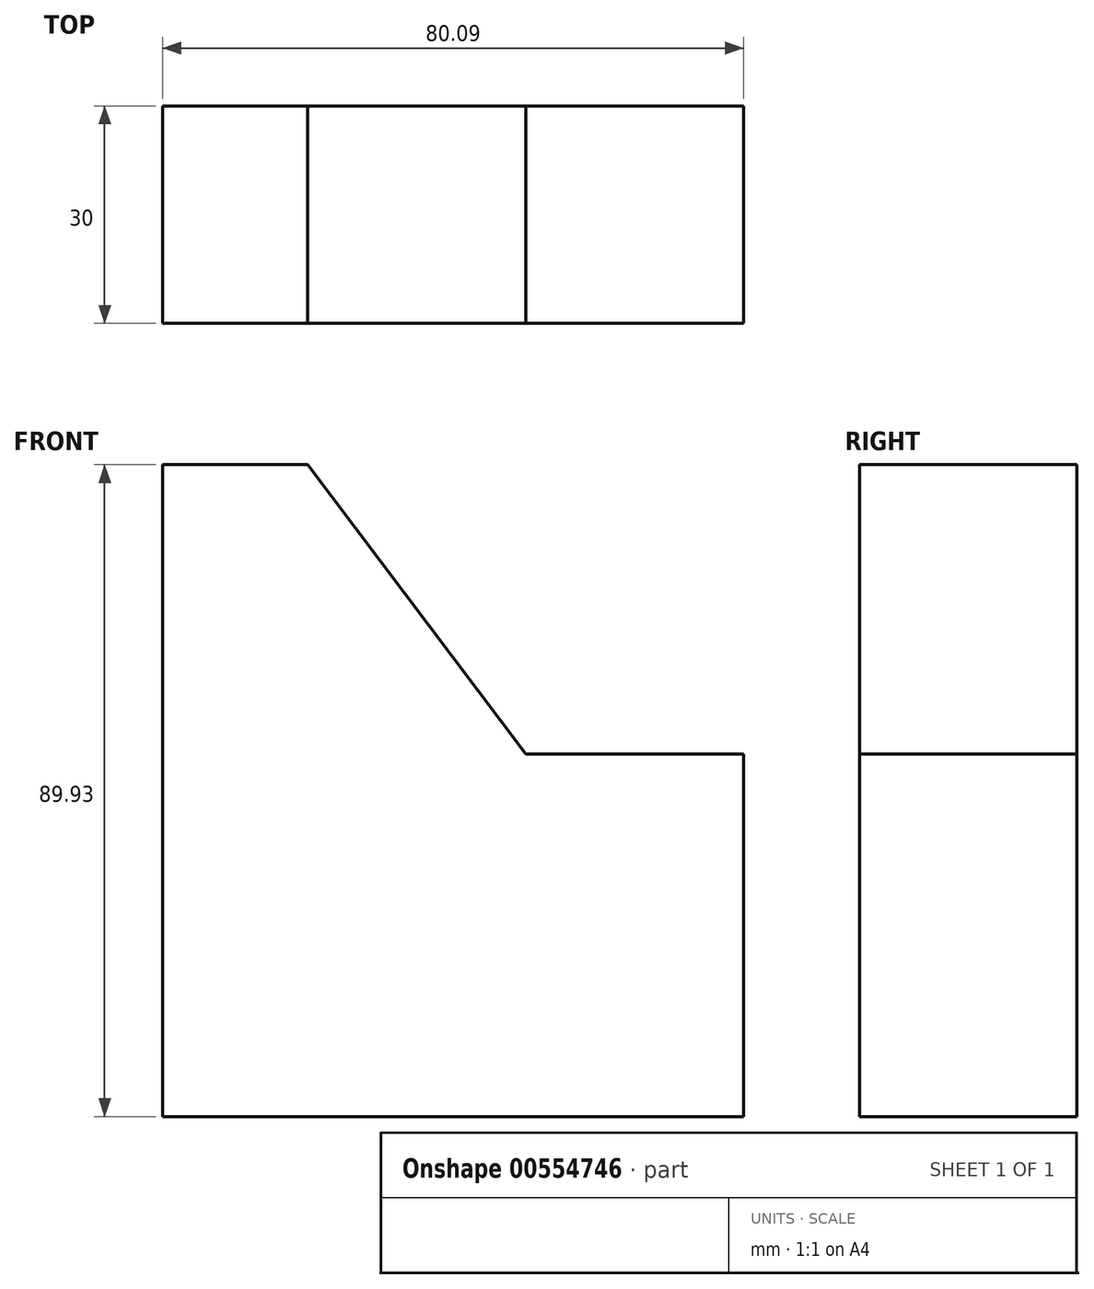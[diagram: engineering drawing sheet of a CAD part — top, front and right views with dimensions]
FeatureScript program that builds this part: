
annotation { "Feature Type Name" : "Feature", "Feature Type Description" : "" }
export const myFeature = defineFeature(function(context is Context, id is Id, definition is map)
    precondition{}
    {
        {
            var Q0;
            Q0=qCreatedBy(makeId("Front.planeOp"),FACE);
            var sketch = newSketch(context, id + "F0", { "sketchPlane" : qUnion([Q0])});
            skLineSegment(sketch, "E0", {"start": v(-57.98, -56.23) * mm, "end": v(22.1, -56.23) * mm});
            skLineSegment(sketch, "E1", {"start": v(-57.98, -56.23) * mm, "end": v(-57.98, 33.7) * mm});
            skLineSegment(sketch, "E2", {"start": v(22.1, -56.23) * mm, "end": v(22.1, -6.23) * mm});
            skLineSegment(sketch, "E3", {"start": v(22.1, -6.23) * mm, "end": v(-7.9, -6.23) * mm});
            skLineSegment(sketch, "E4", {"start": v(-7.9, -6.23) * mm, "end": v(-37.98, 33.7) * mm});
            skLineSegment(sketch, "E5", {"start": v(-37.98, 33.7) * mm, "end": v(-57.98, 33.7) * mm});
            skSolve(sketch);
        }
        {
            var Q0;
            Q0 = qSketchRegion(id + "F0", true);
            extrude(context, id + "F1", {"entities" : qUnion([Q0]), "depth" : 30 * mm, "offsetDistance" : 25 * mm});
        }
    });
